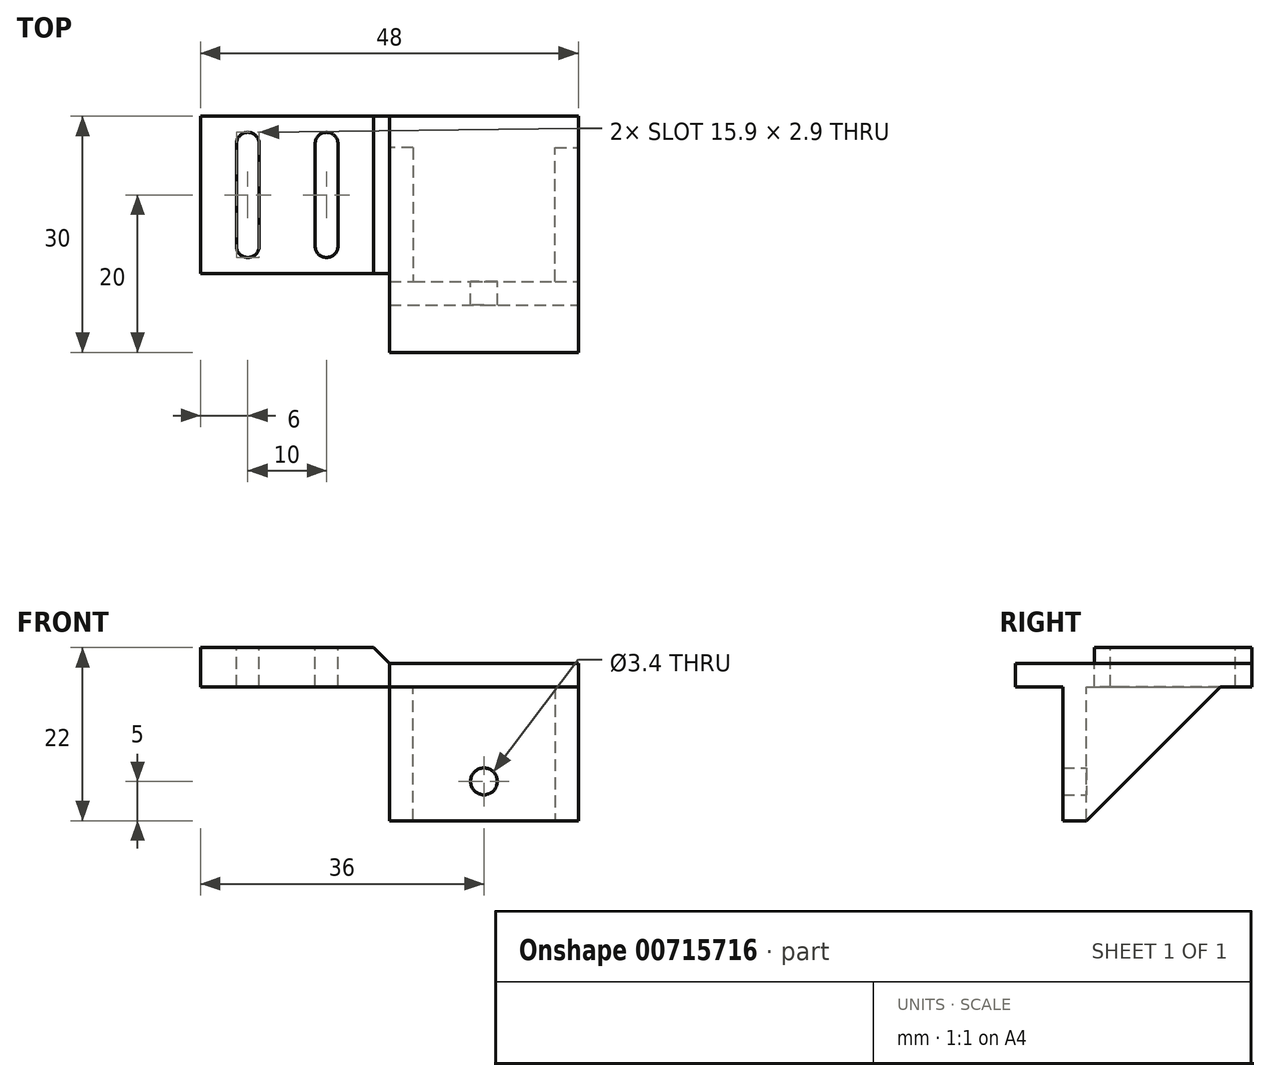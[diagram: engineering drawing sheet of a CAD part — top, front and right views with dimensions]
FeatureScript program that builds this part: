
annotation { "Feature Type Name" : "Feature", "Feature Type Description" : "" }
export const myFeature = defineFeature(function(context is Context, id is Id, definition is map)
    precondition{}
    {
        {
            var Q0;
            Q0=qCreatedBy(makeId("Right.planeOp"),FACE);
            var sketch = newSketch(context, id + "F0", { "sketchPlane" : qUnion([Q0])});
            skLineSegment(sketch, "E0.bottom", {"start": v(-6, 20) * mm, "end": v(24, 20) * mm});
            skLineSegment(sketch, "E0.top", {"start": v(-6, 17) * mm, "end": v(0, 17) * mm});
            skLineSegment(sketch, "E0.left", {"start": v(-6, 20) * mm, "end": v(-6, 17) * mm});
            skLineSegment(sketch, "E0.right", {"start": v(24, 20) * mm, "end": v(24, 17) * mm});
            skLineSegment(sketch, "E1.top", {"start": v(0, 0) * mm, "end": v(3, 0) * mm});
            skLineSegment(sketch, "E1.left", {"start": v(0, 17) * mm, "end": v(0, 0) * mm});
            skLineSegment(sketch, "E1.right", {"start": v(3, 17) * mm, "end": v(3, 0) * mm});
            skLineSegment(sketch, "E2.trimOffspring", {"start": v(3, 17) * mm, "end": v(24, 17) * mm});
            skLineSegment(sketch, "E3", {"start": v(3, 0) * mm, "end": v(20, 17) * mm});
            skSolve(sketch);
        }
        {
            var Q0;
            Q0=makeQuery(id+"F0.imprint","IMPRINT",FACE,{"disambiguationData":[TD([[makeQuery(id+"F0.imprint","IMPRINT",EDGE,{"derivedFrom":sQuery(id+"F0.wireOp",EDGE,"E0.bottom")}),-1.0]])]});
            extrude(context, id + "F1", {"entities" : qUnion([Q0]), "oppositeDirection" : true, "depth" : 48 * mm, "offsetDistance" : 25 * mm});
        }
        {
            var Q0;
            {var subQ0=sQuery(id+"F0.wireOp",EDGE,"E1.right");Q0=makeQuery(id+"F0.imprint","IMPRINT",FACE,{"disambiguationData":[TD([[makeQuery(id+"F0.imprint","IMPRINT",EDGE,{"derivedFrom":subQ0}),1.0]])]});}
            extrude(context, id + "F2", {"entities" : qUnion([Q0]), "operationType" : NewBodyOperationType.ADD, "oppositeDirection" : true, "depth" : 3 * mm, "offsetDistance" : 25 * mm});
        }
        {
            var Q0;
            Q0=makeQuery(id+"F1.opExtrude","SWEPT_FACE",FACE,{"disambiguationData":[OSD([sQuery(id+"F0.wireOp",EDGE,"E0.bottom")])]});
            var sketch = newSketch(context, id + "F3", { "sketchPlane" : qUnion([Q0])});
            skLineSegment(sketch, "E4.bottom", {"start": v(-48, -6) * mm, "end": v(-24, -6) * mm});
            skLineSegment(sketch, "E4.top", {"start": v(-48, 4) * mm, "end": v(-24, 4) * mm});
            skLineSegment(sketch, "E4.left", {"start": v(-48, -6) * mm, "end": v(-48, 4) * mm});
            skLineSegment(sketch, "E4.right", {"start": v(-24, -6) * mm, "end": v(-24, 4) * mm});
            skSolve(sketch);
        }
        {
            var Q0;
            Q0=makeQuery(id+"F3.imprint","IMPRINT",FACE,{"disambiguationData":[TD([[makeQuery(id+"F3.imprint","IMPRINT",EDGE,{"derivedFrom":sQuery(id+"F3.wireOp",EDGE,"E4.bottom")}),1.0]])]});
            extrude(context, id + "F4", {"entities" : qUnion([Q0]), "operationType" : NewBodyOperationType.REMOVE, "oppositeDirection" : true, "depth" : 25 * mm, "offsetDistance" : 25 * mm});
        }
        {
            var Q0;
            Q0=makeQuery(id+"F4.boolean.opBoolean","COPY",FACE,{"derivedFrom":makeQuery(id+"F4.opExtrude","SWEPT_FACE",FACE,{"disambiguationData":[OSD([sQuery(id+"F3.wireOp",EDGE,"E4.right")])]})});
            var sketch = newSketch(context, id + "F5", { "sketchPlane" : qUnion([Q0])});
            skLineSegment(sketch, "E5", {"start": v(-3, 17) * mm, "end": v(-3, 0) * mm});
            skLineSegment(sketch, "E6", {"start": v(-3, 0) * mm, "end": v(-20, 17) * mm});
            skLineSegment(sketch, "E7", {"start": v(-20, 17) * mm, "end": v(-3, 17) * mm});
            skSolve(sketch);
        }
        {
            var Q0;
            {var subQ0=sQuery(id+"F5.wireOp",EDGE,"E5");Q0=makeQuery(id+"F5.imprint","IMPRINT",FACE,{"disambiguationData":[TD([[makeQuery(id+"F5.imprint","IMPRINT",EDGE,{"derivedFrom":subQ0}),1.0]])]});}
            extrude(context, id + "F6", {"entities" : qUnion([Q0]), "operationType" : NewBodyOperationType.ADD, "oppositeDirection" : true, "depth" : 3 * mm, "offsetDistance" : 25 * mm});
        }
        {
            var Q0;
            Q0=makeQuery(id+"F1.opExtrude","SWEPT_FACE",FACE,{"disambiguationData":[OSD([sQuery(id+"F0.wireOp",EDGE,"E1.right")])]});
            var sketch = newSketch(context, id + "F7", { "sketchPlane" : qUnion([Q0])});
            skCircle(sketch, "E8", {"center": v(12, 5) * mm, "radius": 1.7 * mm});
            skLineSegment(sketch, "E9", {"start": v(12, 0) * mm, "end": v(12, 17) * mm, "construction": true});
            skSolve(sketch);
        }
        {
            var Q0;
            Q0=makeQuery(id+"F7.imprint","IMPRINT",FACE,{"disambiguationData":[TD([[makeQuery(id+"F7.imprint","IMPRINT",EDGE,{"derivedFrom":sQuery(id+"F7.wireOp",EDGE,"E8")}),1.0]])]});
            extrude(context, id + "F8", {"entities" : qUnion([Q0]), "operationType" : NewBodyOperationType.REMOVE, "endBound" : BoundingType.THROUGH_ALL, "oppositeDirection" : true, "depth" : 25 * mm, "offsetDistance" : 25 * mm});
        }
        {
            var Q0;
            Q0=makeQuery(id+"F4.boolean.opBoolean","COPY",FACE,{"derivedFrom":makeQuery(id+"F4.opExtrude","SWEPT_FACE",FACE,{"disambiguationData":[OSD([sQuery(id+"F3.wireOp",EDGE,"E4.top")])]})});
            var sketch = newSketch(context, id + "F9", { "sketchPlane" : qUnion([Q0])});
            skLineSegment(sketch, "E10", {"start": v(-24, 20) * mm, "end": v(-26, 22) * mm});
            skLineSegment(sketch, "E11", {"start": v(-26, 22) * mm, "end": v(-48, 22) * mm});
            skLineSegment(sketch, "E12", {"start": v(-48, 22) * mm, "end": v(-48, 20) * mm});
            skLineSegment(sketch, "E13", {"start": v(-48, 20) * mm, "end": v(-24, 20) * mm});
            skSolve(sketch);
        }
        {
            var Q0;
            Q0=makeQuery(id+"F9.imprint","IMPRINT",FACE,{"disambiguationData":[TD([[makeQuery(id+"F9.imprint","IMPRINT",EDGE,{"derivedFrom":sQuery(id+"F9.wireOp",EDGE,"E10")}),1.0]])]});
            extrude(context, id + "F10", {"entities" : qUnion([Q0]), "operationType" : NewBodyOperationType.ADD, "oppositeDirection" : true, "depth" : 20 * mm, "offsetDistance" : 25 * mm});
        }
        {
            var Q0;
            Q0=makeQuery(id+"F10.opExtrude","SWEPT_FACE",FACE,{"disambiguationData":[OSD([sQuery(id+"F9.wireOp",EDGE,"E11")])]});
            var sketch = newSketch(context, id + "F11", { "sketchPlane" : qUnion([Q0])});
            skArc(sketch, "E14", {"start": v(-30.55, 20.5) * mm, "mid": v(-32, 21.95) * mm, "end": v(-33.45, 20.5) * mm});
            skArc(sketch, "E15", {"start": v(-40.55, 20.5) * mm, "mid": v(-42, 21.95) * mm, "end": v(-43.45, 20.5) * mm});
            skArc(sketch, "E16", {"start": v(-40.55, 7.5) * mm, "mid": v(-42, 6.05) * mm, "end": v(-43.45, 7.5) * mm});
            skArc(sketch, "E17", {"start": v(-30.55, 7.5) * mm, "mid": v(-32, 6.05) * mm, "end": v(-33.45, 7.5) * mm});
            skLineSegment(sketch, "E18", {"start": v(-33.45, 20.5) * mm, "end": v(-33.45, 7.5) * mm});
            skLineSegment(sketch, "E19", {"start": v(-30.55, 20.5) * mm, "end": v(-30.55, 7.5) * mm});
            skLineSegment(sketch, "E20", {"start": v(-43.45, 20.5) * mm, "end": v(-43.45, 7.5) * mm});
            skLineSegment(sketch, "E21", {"start": v(-40.55, 20.5) * mm, "end": v(-40.55, 7.5) * mm});
            skSolve(sketch);
        }
        {
            var Q0;
            Q0=makeQuery(id+"F11.imprint","IMPRINT",FACE,{"disambiguationData":[TD([[makeQuery(id+"F11.imprint","IMPRINT",EDGE,{"derivedFrom":sQuery(id+"F11.wireOp",EDGE,"E15")}),1.0]])]});
            var Q1;
            Q1=makeQuery(id+"F11.imprint","IMPRINT",FACE,{"disambiguationData":[TD([[makeQuery(id+"F11.imprint","IMPRINT",EDGE,{"derivedFrom":sQuery(id+"F11.wireOp",EDGE,"E14")}),1.0]])]});
            extrude(context, id + "F12", {"entities" : qUnion([Q0, Q1]), "operationType" : NewBodyOperationType.REMOVE, "endBound" : BoundingType.THROUGH_ALL, "oppositeDirection" : true, "depth" : 25 * mm, "offsetDistance" : 25 * mm});
        }
    });
